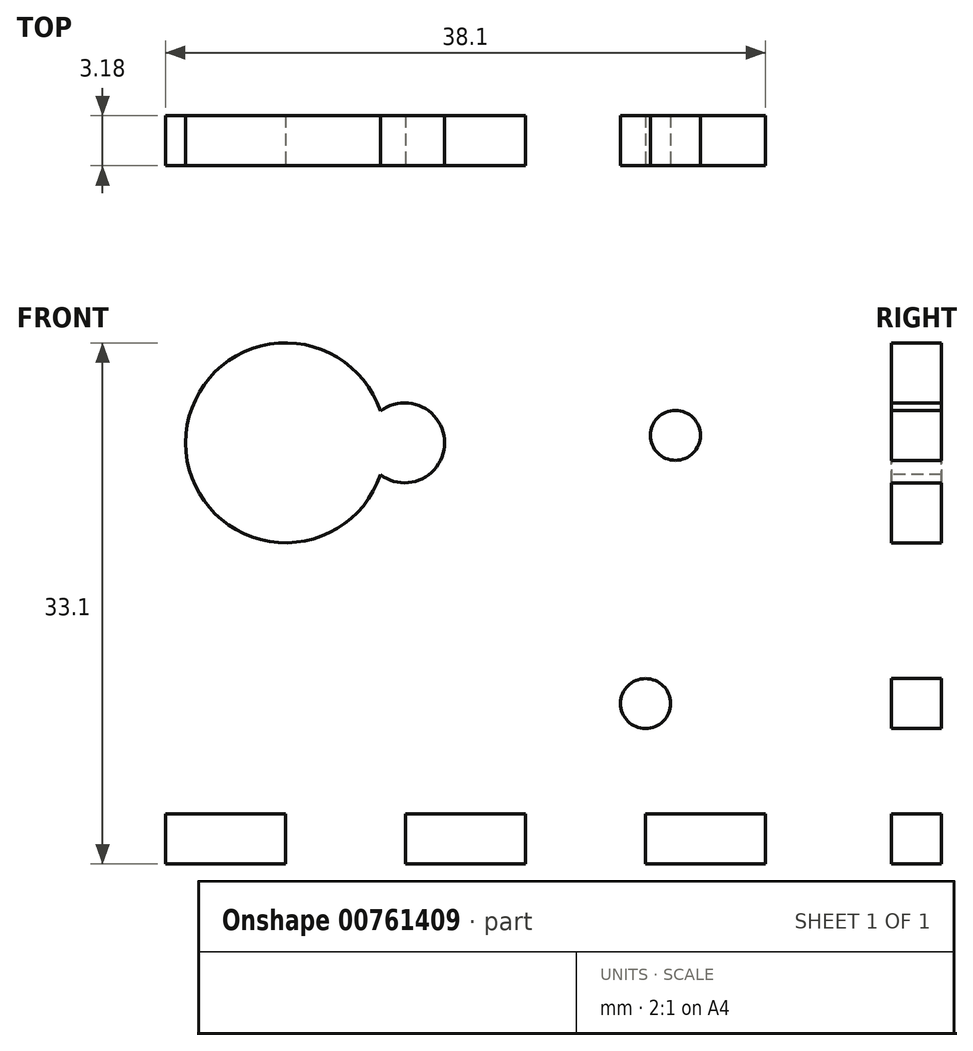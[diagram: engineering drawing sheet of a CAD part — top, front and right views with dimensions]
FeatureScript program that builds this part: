
annotation { "Feature Type Name" : "Feature", "Feature Type Description" : "" }
export const myFeature = defineFeature(function(context is Context, id is Id, definition is map)
    precondition{}
    {
        {
            var Q0;
            Q0=qCreatedBy(makeId("Front.planeOp"),FACE);
            var sketch = newSketch(context, id + "F0", { "sketchPlane" : qUnion([Q0])});
            skPoint(sketch, "E0.middle", {"position": v(0, 0) * mm});
            skLineSegment(sketch, "E1.bottom", {"start": v(-25.26, 16.76) * mm, "end": v(12.84, 16.76) * mm});
            skLineSegment(sketch, "E1.top", {"start": v(-25.26, -21.34) * mm, "end": v(12.84, -21.34) * mm});
            skLineSegment(sketch, "E1.left", {"start": v(-25.26, 16.76) * mm, "end": v(-25.26, -21.34) * mm});
            skLineSegment(sketch, "E1.right", {"start": v(12.84, 16.76) * mm, "end": v(12.84, -21.34) * mm});
            skSolve(sketch);
        }
        {
            var Q0;
            Q0=qSketchRegion(id+"F0",true);
            extrude(context, id + "F1", {"entities" : qUnion([Q0]), "depth" : 3.17 * mm, "offsetDistance" : 25.4 * mm});
        }
        {
            var Q0;
            Q0=makeQuery(id+"F1.opExtrude","CAP_FACE",FACE,{"disambiguationData":[OSD([sQuery(id+"F0.wireOp",EDGE,"E1.bottom"),sQuery(id+"F0.wireOp",EDGE,"E1.top"),sQuery(id+"F0.wireOp",EDGE,"E1.left"),sQuery(id+"F0.wireOp",EDGE,"E1.right")])],"isStart":false});
            var sketch = newSketch(context, id + "F2", { "sketchPlane" : qUnion([Q0])});
            skLineSegment(sketch, "E2.MirrorCS", {"start": v(-2.4, -21.34) * mm, "end": v(-10.02, -21.34) * mm});
            skLineSegment(sketch, "E3.MirrorCS", {"start": v(-17.64, -21.34) * mm, "end": v(-25.26, -21.34) * mm});
            skLineSegment(sketch, "E4.MirrorCS", {"start": v(12.84, -18.16) * mm, "end": v(12.84, -21.34) * mm});
            skLineSegment(sketch, "E5.MirrorCS", {"start": v(12.84, -21.34) * mm, "end": v(5.22, -21.34) * mm});
            skLineSegment(sketch, "E6.MirrorCS", {"start": v(5.22, -18.16) * mm, "end": v(5.22, -21.34) * mm});
            skCircle(sketch, "E7.MirrorC", {"center": v(7.13, 5.88) * mm, "radius": 1.59 * mm});
            skArc(sketch, "E8.MirrorCS", {"start": v(-11.61, 7.43) * mm, "mid": v(-7.53, 5.4) * mm, "end": v(-11.61, 3.39) * mm});
            skArc(sketch, "E9.MirrorCS", {"start": v(-11.61, 3.39) * mm, "mid": v(-23.99, 5.4) * mm, "end": v(-11.61, 7.43) * mm});
            skLineSegment(sketch, "E10.MirrorCS", {"start": v(12.84, 16.76) * mm, "end": v(12.84, -21.34) * mm});
            skLineSegment(sketch, "E11.MirrorCS", {"start": v(12.84, -21.34) * mm, "end": v(-25.26, -21.34) * mm});
            skLineSegment(sketch, "E12.MirrorCS", {"start": v(12.84, 16.76) * mm, "end": v(-25.26, 16.76) * mm});
            skLineSegment(sketch, "E13.MirrorCS", {"start": v(-10.02, -18.16) * mm, "end": v(-10.02, -21.34) * mm});
            skLineSegment(sketch, "E14.MirrorCS", {"start": v(-2.4, -18.16) * mm, "end": v(-2.4, -21.34) * mm});
            skLineSegment(sketch, "E15.MirrorCS", {"start": v(-10.02, -18.16) * mm, "end": v(-17.64, -18.16) * mm});
            skLineSegment(sketch, "E16.MirrorCS", {"start": v(-17.64, -18.16) * mm, "end": v(-25.26, -18.16) * mm});
            skLineSegment(sketch, "E17.MirrorCS", {"start": v(-17.64, -18.16) * mm, "end": v(-17.64, -21.34) * mm});
            skCircle(sketch, "E18.MirrorC", {"center": v(5.22, -11.16) * mm, "radius": 1.59 * mm});
            skLineSegment(sketch, "E19.MirrorCS", {"start": v(12.84, -18.16) * mm, "end": v(5.22, -18.16) * mm});
            skLineSegment(sketch, "E20.MirrorCS", {"start": v(5.22, -18.16) * mm, "end": v(-2.4, -18.16) * mm});
            skLineSegment(sketch, "E21.MirrorCS", {"start": v(-2.4, -18.16) * mm, "end": v(-10.02, -18.16) * mm});
            skLineSegment(sketch, "E22", {"start": v(-25.26, 16.76) * mm, "end": v(-25.26, -21.34) * mm});
            skSolve(sketch);
        }
        {
            var Q0;
            {var subQ0=sQuery(id+"F2.wireOp",EDGE,"E13.MirrorCS");Q0=makeQuery(id+"F2.imprint","IMPRINT",FACE,{"disambiguationData":[TD([[makeQuery(id+"F2.imprint","IMPRINT",EDGE,{"derivedFrom":subQ0}),-1.0]])]});}
            var Q1;
            {var subQ0=sQuery(id+"F2.wireOp",EDGE,"E6.MirrorCS");Q1=makeQuery(id+"F2.imprint","IMPRINT",FACE,{"disambiguationData":[TD([[makeQuery(id+"F2.imprint","IMPRINT",EDGE,{"derivedFrom":subQ0}),-1.0]])]});}
            var Q2;
            Q2=makeQuery(id+"F2.imprint","IMPRINT",FACE,{"disambiguationData":[TD([[makeQuery(id+"F2.imprint","IMPRINT",EDGE,{"derivedFrom":sQuery(id+"F2.wireOp",EDGE,"E7.MirrorC")}),-1.0]])]});
            var Q3;
            Q3=makeQuery(id+"F2.imprint","IMPRINT",FACE,{"disambiguationData":[TD([[makeQuery(id+"F2.imprint","IMPRINT",EDGE,{"derivedFrom":sQuery(id+"F2.wireOp",EDGE,"E18.MirrorC")}),-1.0]])]});
            extrude(context, id + "F3", {"entities" : qUnion([Q0, Q1, Q2, Q3]), "operationType" : NewBodyOperationType.REMOVE, "oppositeDirection" : true, "depth" : 3.17 * mm, "offsetDistance" : 25.4 * mm});
        }
    });
